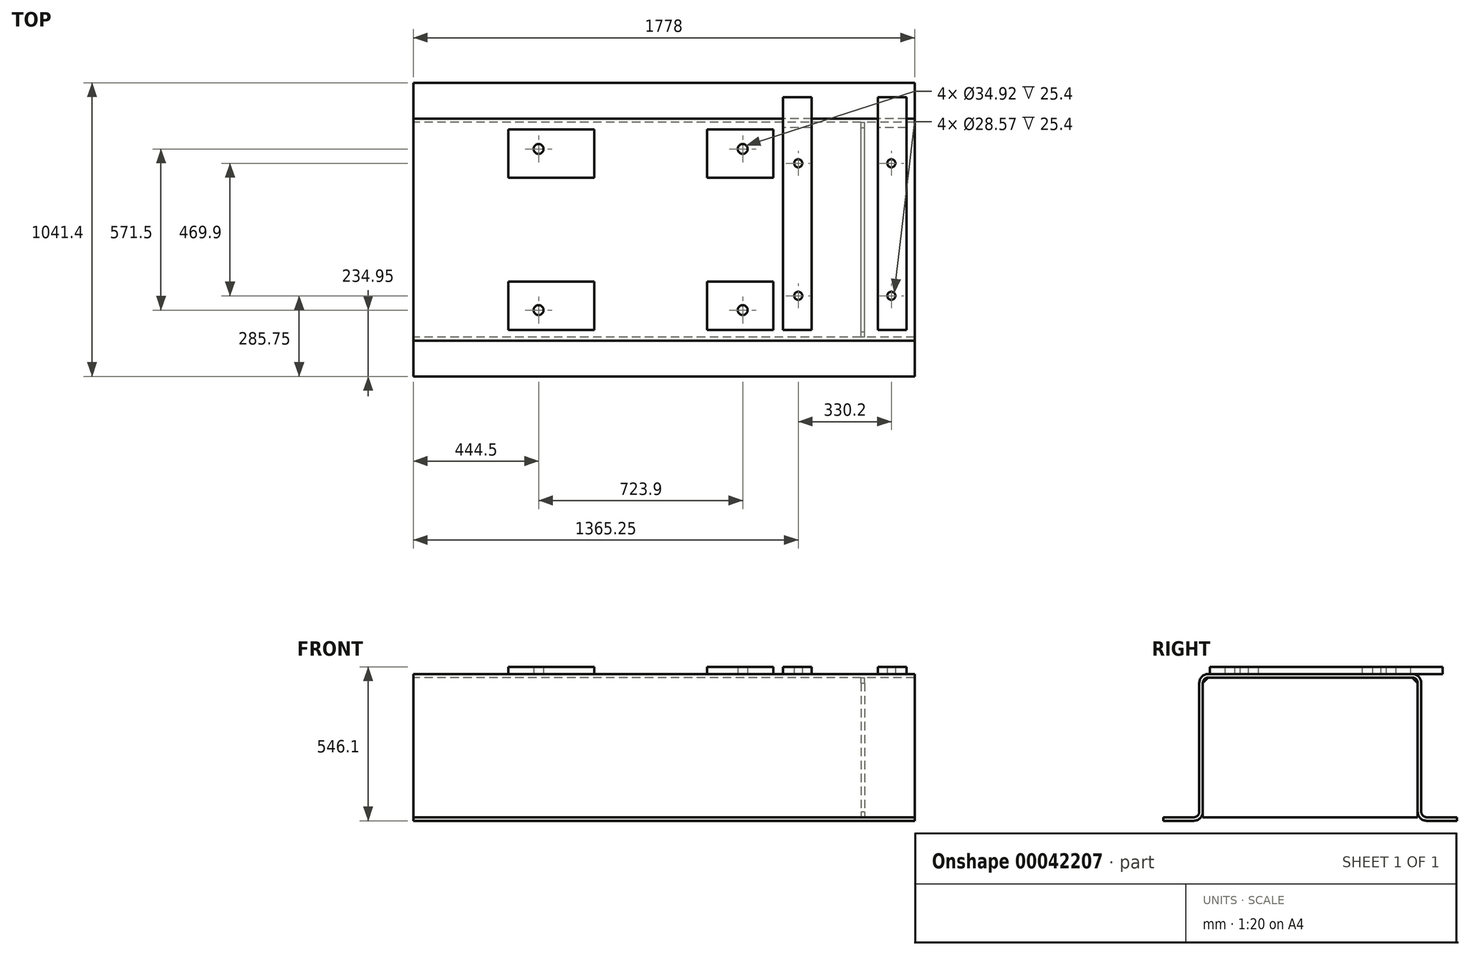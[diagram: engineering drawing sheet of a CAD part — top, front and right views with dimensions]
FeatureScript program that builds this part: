
annotation { "Feature Type Name" : "Feature", "Feature Type Description" : "" }
export const myFeature = defineFeature(function(context is Context, id is Id, definition is map)
    precondition{}
    {
        {
            var Q0;
            Q0=qCreatedBy(makeId("Right.planeOp"),FACE);
            var sketch = newSketch(context, id + "F0", { "sketchPlane" : qUnion([Q0])});
            skLineSegment(sketch, "E0.rect.bottom", {"start": v(-361.95, 260.35) * mm, "end": v(0, 260.35) * mm});
            skLineSegment(sketch, "E0.rect.top", {"start": v(-520.7, -260.35) * mm, "end": v(-412.75, -260.35) * mm});
            skLineSegment(sketch, "E0.rect.left", {"start": v(-393.7, 228.6) * mm, "end": v(-393.7, -228.6) * mm});
            skPoint(sketch, "E0.rect.middle", {"position": v(0, 0) * mm});
            skLineSegment(sketch, "E1", {"start": v(0, 334.43) * mm, "end": v(0, -368.46) * mm, "construction": true});
            skLineSegment(sketch, "E2.0", {"start": v(-520.7, -247.65) * mm, "end": v(-520.7, -260.35) * mm});
            skLineSegment(sketch, "E3.0", {"start": v(-520.7, -247.65) * mm, "end": v(-412.75, -247.65) * mm});
            skLineSegment(sketch, "E4.0", {"start": v(-381, 228.6) * mm, "end": v(-381, -228.6) * mm});
            skLineSegment(sketch, "E5.0", {"start": v(-361.95, 247.65) * mm, "end": v(0, 247.65) * mm});
            skPoint(sketch, "E0.rect.right.end.orphan", {"position": v(393.7, -260.35) * mm});
            skPoint(sketch, "E0.rect.right.start.orphan", {"position": v(393.7, 260.35) * mm});
            skPoint(sketch, "E6.orphan", {"position": v(-393.7, -260.35) * mm});
            skPoint(sketch, "E7.visualSharp", {"position": v(-381, 247.65) * mm});
            skArc(sketch, "E7.filletArc", {"start": v(-361.95, 247.65) * mm, "mid": v(-375.42, 242.07) * mm, "end": v(-381, 228.6) * mm});
            skPoint(sketch, "E8.visualSharp", {"position": v(-393.7, -247.65) * mm});
            skArc(sketch, "E8.filletArc", {"start": v(-412.75, -247.65) * mm, "mid": v(-399.28, -242.07) * mm, "end": v(-393.7, -228.6) * mm});
            skPoint(sketch, "E9.visualSharp", {"position": v(-393.7, 260.35) * mm});
            skArc(sketch, "E9.filletArc", {"start": v(-361.95, 260.35) * mm, "mid": v(-384.4, 251.05) * mm, "end": v(-393.7, 228.6) * mm});
            skPoint(sketch, "E10.visualSharp", {"position": v(-381, -260.35) * mm});
            skArc(sketch, "E10.filletArc", {"start": v(-412.75, -260.35) * mm, "mid": v(-390.3, -251.05) * mm, "end": v(-381, -228.6) * mm});
            skLineSegment(sketch, "E11.MirrorCS", {"start": v(520.7, -247.65) * mm, "end": v(520.7, -260.35) * mm});
            skArc(sketch, "E12.MirrorCS", {"start": v(412.75, -247.65) * mm, "mid": v(399.28, -242.07) * mm, "end": v(393.7, -228.6) * mm});
            skArc(sketch, "E13.MirrorCS", {"start": v(361.95, 247.65) * mm, "mid": v(375.42, 242.07) * mm, "end": v(381, 228.6) * mm});
            skArc(sketch, "E14.MirrorCS", {"start": v(412.75, -260.35) * mm, "mid": v(390.3, -251.05) * mm, "end": v(381, -228.6) * mm});
            skPoint(sketch, "E15.MirrorP", {"position": v(393.7, -247.65) * mm});
            skArc(sketch, "E16.MirrorCS", {"start": v(361.95, 260.35) * mm, "mid": v(384.4, 251.05) * mm, "end": v(393.7, 228.6) * mm});
            skLineSegment(sketch, "E17.MirrorCS", {"start": v(361.95, 260.35) * mm, "end": v(0, 260.35) * mm});
            skLineSegment(sketch, "E18.MirrorCS", {"start": v(520.7, -260.35) * mm, "end": v(412.75, -260.35) * mm});
            skLineSegment(sketch, "E19.MirrorCS", {"start": v(393.7, 228.6) * mm, "end": v(393.7, -228.6) * mm});
            skLineSegment(sketch, "E20.MirrorCS", {"start": v(520.7, -247.65) * mm, "end": v(412.75, -247.65) * mm});
            skPoint(sketch, "E21.MirrorP", {"position": v(381, -260.35) * mm});
            skPoint(sketch, "E22.MirrorP", {"position": v(381, 247.65) * mm});
            skLineSegment(sketch, "E23.MirrorCS", {"start": v(361.95, 247.65) * mm, "end": v(0, 247.65) * mm});
            skLineSegment(sketch, "E24.MirrorCS", {"start": v(381, 228.6) * mm, "end": v(381, -228.6) * mm});
            skSolve(sketch);
        }
        {
            var Q0;
            Q0 = qSketchRegion(id + "F0", true);
            extrude(context, id + "F1", {"entities" : qUnion([Q0]), "endBound" : BoundingType.SYMMETRIC, "depth" : 1778 * mm});
        }
        {
            var Q0;
            Q0=makeQuery(id+"F1.opExtrude","SWEPT_FACE",FACE,{"disambiguationData":[OSD([sQuery(id+"F0.wireOp",EDGE,"E0.rect.bottom"),sQuery(id+"F0.wireOp",EDGE,"E17.MirrorCS")])]});
            var sketch = newSketch(context, id + "F2", { "sketchPlane" : qUnion([Q0])});
            skLineSegment(sketch, "E25", {"start": v(-1218.48, 0) * mm, "end": v(1193.9, 0) * mm, "construction": true});
            skLineSegment(sketch, "E26.0", {"start": v(641.35, -361.95) * mm, "end": v(641.35, 361.95) * mm, "construction": true});
            skLineSegment(sketch, "E27.0", {"start": v(-82.55, -361.95) * mm, "end": v(-82.55, 361.95) * mm, "construction": true});
            skLineSegment(sketch, "E28.0", {"start": v(152.4, -361.95) * mm, "end": v(152.4, -184.15) * mm});
            skLineSegment(sketch, "E29.0", {"start": v(387.35, -361.95) * mm, "end": v(387.35, -184.15) * mm});
            skLineSegment(sketch, "E30.0", {"start": v(-247.65, -361.95) * mm, "end": v(-247.65, -184.15) * mm});
            skLineSegment(sketch, "E31.0", {"start": v(-552.45, -361.95) * mm, "end": v(-552.45, -184.15) * mm});
            skLineSegment(sketch, "E32.0", {"start": v(-552.45, -184.15) * mm, "end": v(-247.65, -184.15) * mm});
            skLineSegment(sketch, "E33.0", {"start": v(-552.45, -355.6) * mm, "end": v(-247.65, -355.6) * mm});
            skLineSegment(sketch, "E34.trimOffspring", {"start": v(152.4, -184.15) * mm, "end": v(387.35, -184.15) * mm});
            skLineSegment(sketch, "E35.trimOffspring", {"start": v(152.4, -355.6) * mm, "end": v(387.35, -355.6) * mm});
            skLineSegment(sketch, "E36.0", {"start": v(-1218.48, -285.75) * mm, "end": v(1193.9, -285.75) * mm, "construction": true});
            skLineSegment(sketch, "E37.0", {"start": v(-444.5, -361.95) * mm, "end": v(-444.5, 361.95) * mm, "construction": true});
            skLineSegment(sketch, "E38.0", {"start": v(279.4, -361.95) * mm, "end": v(279.4, 361.95) * mm, "construction": true});
            skCircle(sketch, "E39", {"center": v(-444.5, -285.75) * mm, "radius": 17.46 * mm});
            skCircle(sketch, "E40", {"center": v(279.4, -285.75) * mm, "radius": 17.46 * mm});
            skLineSegment(sketch, "E41.MirrorCS", {"start": v(-552.45, 184.15) * mm, "end": v(-247.65, 184.15) * mm});
            skLineSegment(sketch, "E42.MirrorCS", {"start": v(-552.45, 361.95) * mm, "end": v(-552.45, 184.15) * mm});
            skLineSegment(sketch, "E43.MirrorCS", {"start": v(-247.65, 361.95) * mm, "end": v(-247.65, 184.15) * mm});
            skCircle(sketch, "E44.MirrorC", {"center": v(279.4, 285.75) * mm, "radius": 17.46 * mm});
            skLineSegment(sketch, "E45.MirrorCS", {"start": v(152.4, 355.6) * mm, "end": v(387.35, 355.6) * mm});
            skLineSegment(sketch, "E46.MirrorCS", {"start": v(152.4, 361.95) * mm, "end": v(152.4, 184.15) * mm});
            skCircle(sketch, "E47.MirrorC", {"center": v(-444.5, 285.75) * mm, "radius": 17.46 * mm});
            skLineSegment(sketch, "E48.MirrorCS", {"start": v(387.35, 361.95) * mm, "end": v(387.35, 184.15) * mm});
            skLineSegment(sketch, "E49.MirrorCS", {"start": v(152.4, 184.15) * mm, "end": v(387.35, 184.15) * mm});
            skLineSegment(sketch, "E50.MirrorCS", {"start": v(-552.45, 355.6) * mm, "end": v(-247.65, 355.6) * mm});
            skSolve(sketch);
        }
        {
            var Q0;
            Q0 = qSketchRegion(id + "F2", true);
            extrude(context, id + "F3", {"entities" : qUnion([Q0]), "operationType" : NewBodyOperationType.ADD, "depth" : 25.4 * mm});
        }
        {
            var Q0;
            {var subQ20=sQuery(id+"F2.wireOp",EDGE,"E32.0");Q0=makeQuery(id+"F2.imprint","IMPRINT",FACE,{"disambiguationData":[TD([[makeQuery(id+"F2.imprint","IMPRINT",EDGE,{"derivedFrom":subQ20}),1.0]])]});}
            var sketch = newSketch(context, id + "F4", { "sketchPlane" : qUnion([Q0])});
            skLineSegment(sketch, "E51.0", {"start": v(-1218.48, 0) * mm, "end": v(1193.9, 0) * mm, "construction": true});
            skLineSegment(sketch, "E52.0", {"start": v(641.35, -361.95) * mm, "end": v(641.35, 361.95) * mm, "construction": true});
            skLineSegment(sketch, "E53.0", {"start": v(-1218.48, -317.5) * mm, "end": v(1193.9, -317.5) * mm, "construction": true});
            skLineSegment(sketch, "E54.0", {"start": v(-1218.48, 469.9) * mm, "end": v(1193.9, 469.9) * mm, "construction": true});
            skLineSegment(sketch, "E55.0", {"start": v(758.95, -361.95) * mm, "end": v(758.95, 361.95) * mm, "construction": true});
            skLineSegment(sketch, "E56.0", {"start": v(524, -361.95) * mm, "end": v(524, 361.95) * mm, "construction": true});
            skLineSegment(sketch, "E57.0", {"start": v(422.4, -361.95) * mm, "end": v(422.4, 361.95) * mm, "construction": true});
            skLineSegment(sketch, "E58.0", {"start": v(-241.3, -177.8) * mm, "end": v(-241.3, -355.6) * mm, "construction": true});
            skLineSegment(sketch, "E58.1", {"start": v(-558.8, -177.8) * mm, "end": v(-241.3, -177.8) * mm, "construction": true});
            skLineSegment(sketch, "E58.2", {"start": v(-558.8, -355.6) * mm, "end": v(-558.8, -177.8) * mm, "construction": true});
            skLineSegment(sketch, "E58.3", {"start": v(-882.65, -355.6) * mm, "end": v(-558.8, -355.6) * mm, "construction": true});
            skLineSegment(sketch, "E58.4", {"start": v(-882.65, 355.6) * mm, "end": v(-882.65, -355.6) * mm, "construction": true});
            skLineSegment(sketch, "E58.5", {"start": v(-241.3, -355.6) * mm, "end": v(146.05, -355.6) * mm, "construction": true});
            skLineSegment(sketch, "E58.6", {"start": v(-558.8, 355.6) * mm, "end": v(-882.65, 355.6) * mm, "construction": true});
            skLineSegment(sketch, "E58.7", {"start": v(-558.8, 177.8) * mm, "end": v(-558.8, 355.6) * mm, "construction": true});
            skLineSegment(sketch, "E58.8", {"start": v(-241.3, 177.8) * mm, "end": v(-558.8, 177.8) * mm, "construction": true});
            skLineSegment(sketch, "E58.9", {"start": v(-241.3, 355.6) * mm, "end": v(-241.3, 177.8) * mm, "construction": true});
            skLineSegment(sketch, "E58.10", {"start": v(393.7, -355.6) * mm, "end": v(882.65, -355.6) * mm, "construction": true});
            skLineSegment(sketch, "E58.11", {"start": v(393.7, -177.8) * mm, "end": v(393.7, -355.6) * mm, "construction": true});
            skLineSegment(sketch, "E58.12", {"start": v(146.05, -177.8) * mm, "end": v(393.7, -177.8) * mm, "construction": true});
            skLineSegment(sketch, "E58.13", {"start": v(146.05, -355.6) * mm, "end": v(146.05, -177.8) * mm, "construction": true});
            skLineSegment(sketch, "E58.14", {"start": v(882.65, -355.6) * mm, "end": v(882.65, 355.6) * mm, "construction": true});
            skLineSegment(sketch, "E58.15", {"start": v(882.65, 355.6) * mm, "end": v(393.7, 355.6) * mm, "construction": true});
            skLineSegment(sketch, "E58.16", {"start": v(393.7, 355.6) * mm, "end": v(393.7, 177.8) * mm, "construction": true});
            skLineSegment(sketch, "E58.17", {"start": v(393.7, 177.8) * mm, "end": v(146.05, 177.8) * mm, "construction": true});
            skLineSegment(sketch, "E58.18", {"start": v(146.05, 177.8) * mm, "end": v(146.05, 355.6) * mm, "construction": true});
            skLineSegment(sketch, "E58.19", {"start": v(146.05, 355.6) * mm, "end": v(-241.3, 355.6) * mm, "construction": true});
            skLineSegment(sketch, "E59.bottom", {"start": v(422.4, -355.6) * mm, "end": v(524, -355.6) * mm});
            skLineSegment(sketch, "E59.top", {"start": v(422.4, 469.9) * mm, "end": v(524, 469.9) * mm});
            skLineSegment(sketch, "E59.left", {"start": v(422.4, -355.6) * mm, "end": v(422.4, 469.9) * mm});
            skLineSegment(sketch, "E59.right", {"start": v(524, -355.6) * mm, "end": v(524, 469.9) * mm});
            skLineSegment(sketch, "E60.MirrorCS", {"start": v(860.3, -361.95) * mm, "end": v(860.3, 361.95) * mm});
            skLineSegment(sketch, "E61.MirrorCS", {"start": v(758.7, -361.95) * mm, "end": v(758.7, 361.95) * mm});
            skLineSegment(sketch, "E62.MirrorCS", {"start": v(758.7, -355.6) * mm, "end": v(758.7, 469.9) * mm});
            skLineSegment(sketch, "E63.MirrorCS", {"start": v(889, 355.6) * mm, "end": v(889, 177.8) * mm});
            skLineSegment(sketch, "E64.MirrorCS", {"start": v(860.3, -355.6) * mm, "end": v(860.3, 469.9) * mm});
            skLineSegment(sketch, "E65.MirrorCS", {"start": v(860.3, -355.6) * mm, "end": v(758.7, -355.6) * mm});
            skLineSegment(sketch, "E66.MirrorCS", {"start": v(860.3, 469.9) * mm, "end": v(758.7, 469.9) * mm});
            skLineSegment(sketch, "E67.MirrorCS", {"start": v(889, -177.8) * mm, "end": v(889, -355.6) * mm});
            skLineSegment(sketch, "E68.0", {"start": v(-1218.48, -234.95) * mm, "end": v(1193.9, -234.95) * mm, "construction": true});
            skLineSegment(sketch, "E69.0", {"start": v(806.45, -361.95) * mm, "end": v(806.45, 361.95) * mm, "construction": true});
            skCircle(sketch, "E70", {"center": v(806.45, -234.95) * mm, "radius": 14.29 * mm});
            skCircle(sketch, "E71.MirrorC", {"center": v(476.25, -234.95) * mm, "radius": 14.29 * mm});
            skCircle(sketch, "E72.MirrorC", {"center": v(476.25, 234.95) * mm, "radius": 14.29 * mm});
            skCircle(sketch, "E73.MirrorC", {"center": v(806.45, 234.95) * mm, "radius": 14.29 * mm});
            skSolve(sketch);
        }
        {
            var Q0;
            Q0 = qSketchRegion(id + "F4", true);
            extrude(context, id + "F5", {"entities" : qUnion([Q0]), "operationType" : NewBodyOperationType.ADD, "depth" : 25.4 * mm});
        }
        {
            var Q0;
            Q0=makeQuery(id+"F1.opExtrude","CAP_FACE",FACE,{"disambiguationData":[OSD([sQuery(id+"F0.wireOp",EDGE,"E0.rect.bottom"),sQuery(id+"F0.wireOp",EDGE,"E0.rect.top"),sQuery(id+"F0.wireOp",EDGE,"E0.rect.left"),sQuery(id+"F0.wireOp",EDGE,"E2.0"),sQuery(id+"F0.wireOp",EDGE,"E3.0"),sQuery(id+"F0.wireOp",EDGE,"E4.0"),sQuery(id+"F0.wireOp",EDGE,"E5.0"),sQuery(id+"F0.wireOp",EDGE,"E7.filletArc"),sQuery(id+"F0.wireOp",EDGE,"E8.filletArc"),sQuery(id+"F0.wireOp",EDGE,"E9.filletArc"),sQuery(id+"F0.wireOp",EDGE,"E10.filletArc"),sQuery(id+"F0.wireOp",EDGE,"E11.MirrorCS"),sQuery(id+"F0.wireOp",EDGE,"E12.MirrorCS"),sQuery(id+"F0.wireOp",EDGE,"E13.MirrorCS"),sQuery(id+"F0.wireOp",EDGE,"E14.MirrorCS"),sQuery(id+"F0.wireOp",EDGE,"E16.MirrorCS"),sQuery(id+"F0.wireOp",EDGE,"E17.MirrorCS"),sQuery(id+"F0.wireOp",EDGE,"E18.MirrorCS"),sQuery(id+"F0.wireOp",EDGE,"E19.MirrorCS"),sQuery(id+"F0.wireOp",EDGE,"E20.MirrorCS"),sQuery(id+"F0.wireOp",EDGE,"E23.MirrorCS"),sQuery(id+"F0.wireOp",EDGE,"E24.MirrorCS")])],"isStart":false});
            cPlane(context, id + "F6", {"entities" : qUnion([Q0]), "cplaneType" : CPlaneType.OFFSET, "offset" : 177.8 * mm, "oppositeDirection" : true, "width" : 152.4 * mm, "height" : 152.4 * mm});
        }
        {
            var Q0;
            Q0=qCreatedBy(id+"F6.planeOp",FACE);
            var sketch = newSketch(context, id + "F7", { "sketchPlane" : qUnion([Q0])});
            skLineSegment(sketch, "E74.0", {"start": v(-381, 228.6) * mm, "end": v(-381, -247.65) * mm});
            skLineSegment(sketch, "E75.0", {"start": v(-361.95, 247.65) * mm, "end": v(361.95, 247.65) * mm});
            skLineSegment(sketch, "E76.0", {"start": v(381, 228.6) * mm, "end": v(381, -247.65) * mm});
            skLineSegment(sketch, "E77.0", {"start": v(-520.7, -247.65) * mm, "end": v(-412.75, -247.65) * mm, "construction": true});
            skLineSegment(sketch, "E78", {"start": v(-412.75, -247.65) * mm, "end": v(389.6, -247.65) * mm});
            skLineSegment(sketch, "E79", {"start": v(-381, 228.6) * mm, "end": v(-361.95, 247.65) * mm});
            skLineSegment(sketch, "E80", {"start": v(361.95, 247.65) * mm, "end": v(381, 228.6) * mm});
            skPoint(sketch, "E81.orphan", {"position": v(-381, -228.6) * mm});
            skPoint(sketch, "E82.orphan", {"position": v(381, -228.6) * mm});
            skSolve(sketch);
        }
        {
            var Q0;
            Q0 = qSketchRegion(id + "F7", true);
            extrude(context, id + "F8", {"entities" : qUnion([Q0]), "operationType" : NewBodyOperationType.ADD, "oppositeDirection" : true, "depth" : 12.7 * mm});
        }
    });
